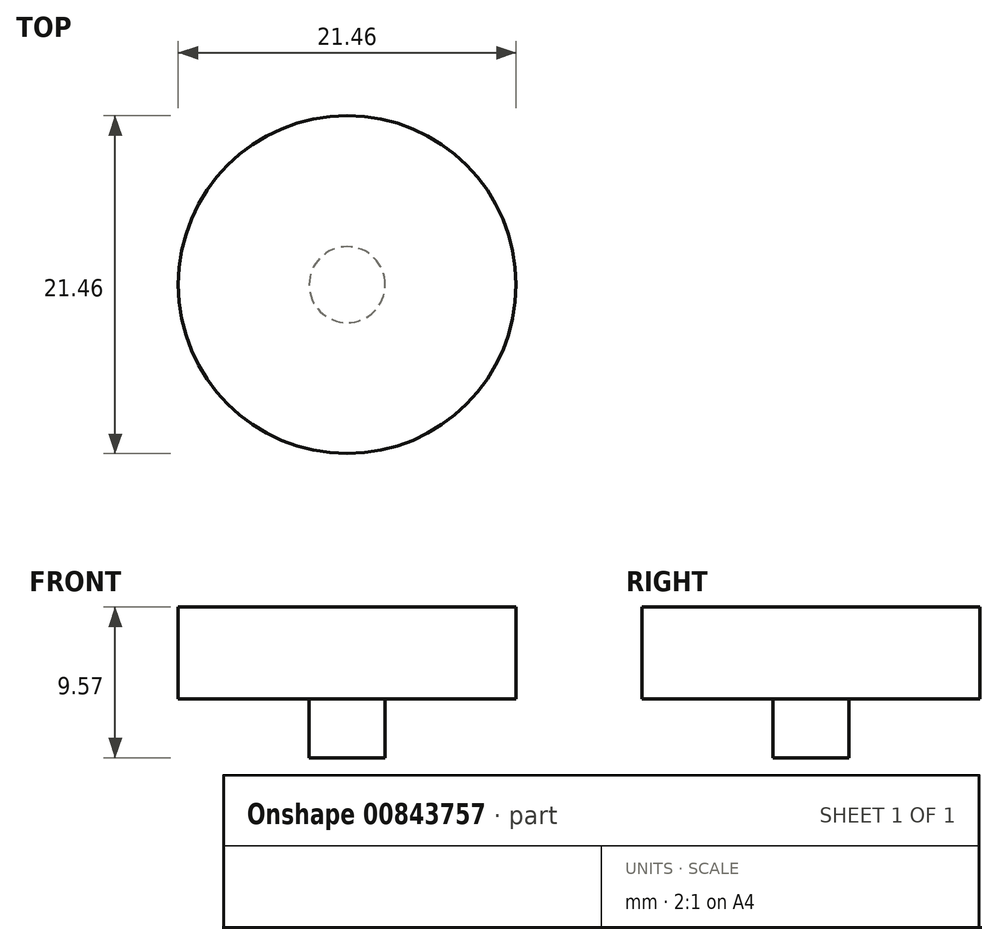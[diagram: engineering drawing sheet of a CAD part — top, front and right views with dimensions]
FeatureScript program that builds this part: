
annotation { "Feature Type Name" : "Feature", "Feature Type Description" : "" }
export const myFeature = defineFeature(function(context is Context, id is Id, definition is map)
    precondition{}
    {
        {
            var Q0;
            Q0=qCreatedBy(makeId("Top.planeOp"),FACE);
            var sketch = newSketch(context, id + "F0", { "sketchPlane" : qUnion([Q0])});
            skCircle(sketch, "E0", {"center": v(0, 0) * mm, "radius": 10.73 * mm});
            skSolve(sketch);
        }
        {
            var Q0;
            Q0=makeQuery(id+"F0.imprint","IMPRINT",FACE,{"disambiguationData":[TD([[makeQuery(id+"F0.imprint","IMPRINT",EDGE,{"derivedFrom":sQuery(id+"F0.wireOp",EDGE,"E0")}),1.0]])]});
            extrude(context, id + "F1", {"entities" : qUnion([Q0]), "depth" : 5.84 * mm, "offsetDistance" : 25.4 * mm});
        }
        {
            var Q0;
            Q0=makeQuery(id+"F0.imprint","IMPRINT",FACE,{"disambiguationData":[TD([[makeQuery(id+"F0.imprint","IMPRINT",EDGE,{"derivedFrom":sQuery(id+"F0.wireOp",EDGE,"E0")}),1.0]])]});
            var sketch = newSketch(context, id + "F2", { "sketchPlane" : qUnion([Q0])});
            skCircle(sketch, "E1", {"center": v(0, 0) * mm, "radius": 2.41 * mm});
            skSolve(sketch);
        }
        {
            var Q0;
            Q0=makeQuery(id+"F2.imprint","IMPRINT",FACE,{"disambiguationData":[TD([[makeQuery(id+"F2.imprint","IMPRINT",EDGE,{"derivedFrom":sQuery(id+"F2.wireOp",EDGE,"E1")}),1.0]])]});
            extrude(context, id + "F3", {"entities" : qUnion([Q0]), "operationType" : NewBodyOperationType.ADD, "oppositeDirection" : true, "depth" : 3.73 * mm, "offsetDistance" : 25.4 * mm});
        }
    });
